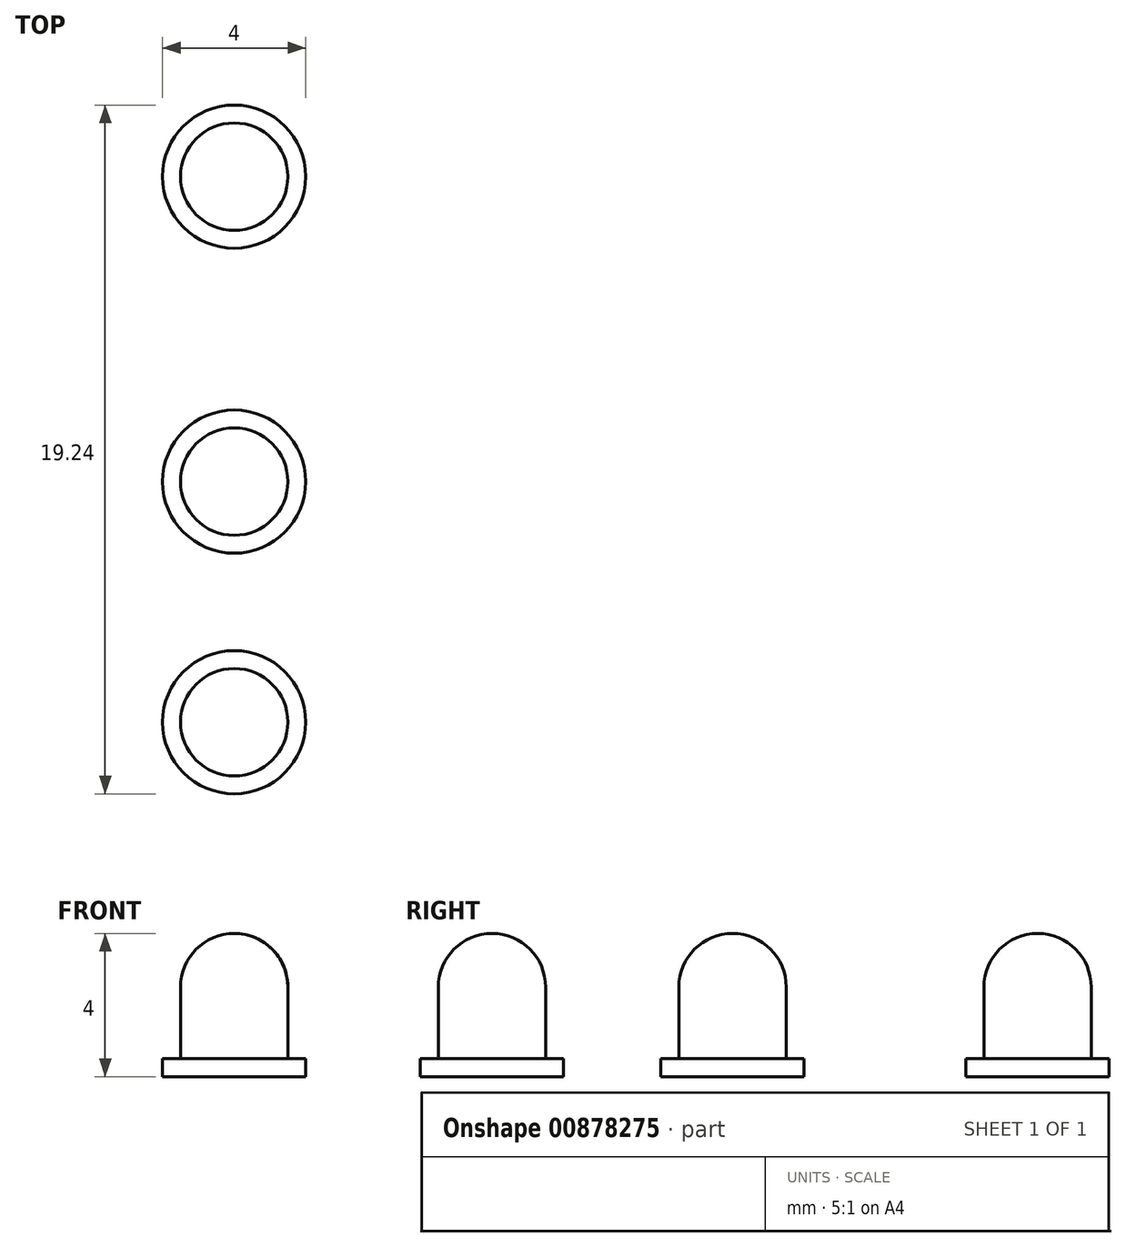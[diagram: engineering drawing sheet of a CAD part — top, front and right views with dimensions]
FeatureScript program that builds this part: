
annotation { "Feature Type Name" : "Feature", "Feature Type Description" : "" }
export const myFeature = defineFeature(function(context is Context, id is Id, definition is map)
    precondition{}
    {
        {
            var Q0;
            Q0=qCreatedBy(makeId("Front.planeOp"),FACE);
            var sketch = newSketch(context, id + "F0", { "sketchPlane" : qUnion([Q0])});
            skLineSegment(sketch, "E0.bottom", {"start": v(-1.5, 0) * mm, "end": v(1.5, 0) * mm});
            skLineSegment(sketch, "E0.left", {"start": v(-1.5, 0.5) * mm, "end": v(-1.5, 2.5) * mm});
            skLineSegment(sketch, "E0.right", {"start": v(1.5, 0.5) * mm, "end": v(1.5, 2.5) * mm});
            skArc(sketch, "E1", {"start": v(1.5, 2.5) * mm, "mid": v(0, 4) * mm, "end": v(-1.5, 2.5) * mm});
            skLineSegment(sketch, "E2.bottom", {"start": v(-2, 0) * mm, "end": v(2, 0) * mm});
            skLineSegment(sketch, "E2.top", {"start": v(-2, 0.5) * mm, "end": v(-1.5, 0.5) * mm});
            skLineSegment(sketch, "E2.left", {"start": v(-2, 0) * mm, "end": v(-2, 0.5) * mm});
            skLineSegment(sketch, "E2.right", {"start": v(2, 0) * mm, "end": v(2, 0.5) * mm});
            skLineSegment(sketch, "E3.trimOffspring", {"start": v(1.5, 0.5) * mm, "end": v(2, 0.5) * mm});
            skLineSegment(sketch, "E4", {"start": v(0, 5.96) * mm, "end": v(0, -0.9) * mm});
            skSolve(sketch);
        }
        {
            var Q0;
            {var subQ5=sQuery(id+"F0.wireOp",EDGE,"E0.right");Q0=makeQuery(id+"F0.imprint","IMPRINT",FACE,{"disambiguationData":[TD([[makeQuery(id+"F0.imprint","IMPRINT",EDGE,{"derivedFrom":subQ5}),1.0]])]});}
            var Q1;
            Q1=sQuery(id+"F0.wireOp",EDGE,"E4");
            revolve(context, id + "F1", {"surfaceOperationType" : NewSurfaceOperationType.NEW, "entities" : qUnion([Q0]), "axis" : qUnion([Q1]), "revolveType" : RevolveType.FULL});
        }
        {
            var Q0;
            Q0=makeQuery(id+"F1.opRevolve","SWEPT_BODY",BODY,{"disambiguationData":[OSD([sQuery(id+"F0.wireOp",EDGE,"E0.right"),sQuery(id+"F0.wireOp",EDGE,"E1"),sQuery(id+"F0.wireOp",EDGE,"E2.bottom"),sQuery(id+"F0.wireOp",EDGE,"E2.right"),sQuery(id+"F0.wireOp",EDGE,"E3.trimOffspring"),sQuery(id+"F0.wireOp",EDGE,"E4")])]});
            transform(context, id + "F2", {"entities" : qUnion([Q0]), "transformType" : TransformType.TRANSLATION_3D, "dx" : 0 * mm, "dy" : 6.72 * mm, "dz" : 0 * mm, "makeCopy" : true});
        }
        {
            var Q0;
            Q0=makeQuery(id+"F2.opPattern","COPY",BODY,{"derivedFrom":makeQuery(id+"F1.opRevolve","SWEPT_BODY",BODY,{"disambiguationData":[OSD([sQuery(id+"F0.wireOp",EDGE,"E0.right"),sQuery(id+"F0.wireOp",EDGE,"E1"),sQuery(id+"F0.wireOp",EDGE,"E2.bottom"),sQuery(id+"F0.wireOp",EDGE,"E2.right"),sQuery(id+"F0.wireOp",EDGE,"E3.trimOffspring"),sQuery(id+"F0.wireOp",EDGE,"E4")])]}),"instanceName":"1"});
            transform(context, id + "F3", {"entities" : qUnion([Q0]), "transformType" : TransformType.TRANSLATION_3D, "dx" : 0 * mm, "dy" : 8.52 * mm, "dz" : 0 * mm, "makeCopy" : true});
        }
    });
